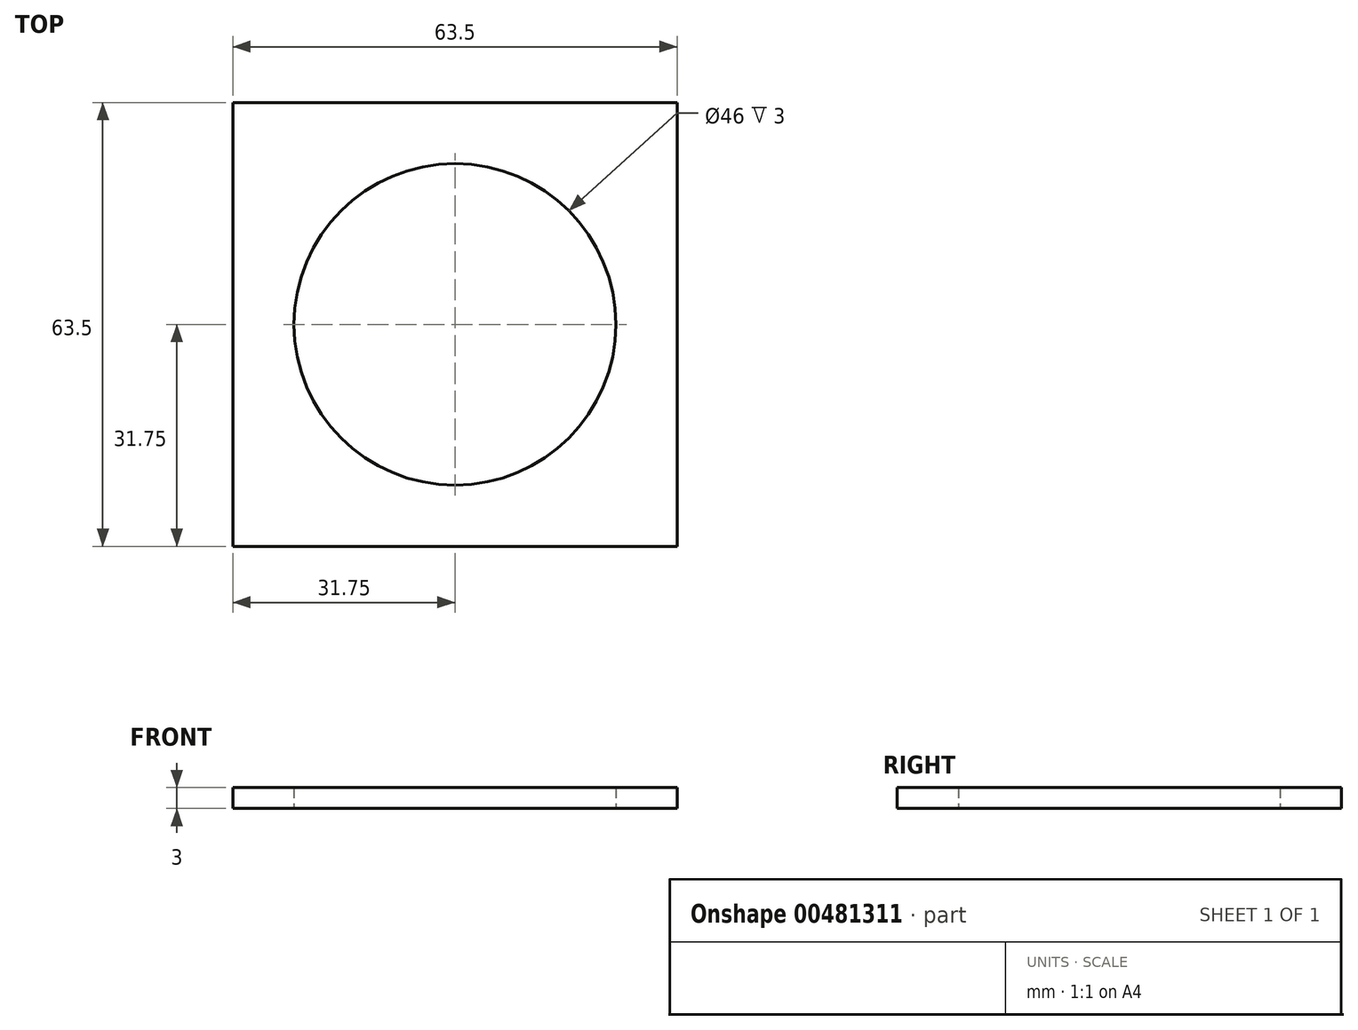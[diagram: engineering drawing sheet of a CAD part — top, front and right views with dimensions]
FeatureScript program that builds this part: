
annotation { "Feature Type Name" : "Feature", "Feature Type Description" : "" }
export const myFeature = defineFeature(function(context is Context, id is Id, definition is map)
    precondition{}
    {
        {
            var Q0;
            Q0=qCreatedBy(makeId("Top.planeOp"),FACE);
            var sketch = newSketch(context, id + "F0", { "sketchPlane" : qUnion([Q0])});
            skCircle(sketch, "E0", {"center": v(0, 0) * mm, "radius": 23 * mm});
            skLineSegment(sketch, "E1.bottom", {"start": v(31.75, 31.75) * mm, "end": v(-31.75, 31.75) * mm});
            skLineSegment(sketch, "E1.top", {"start": v(31.75, -31.75) * mm, "end": v(-31.75, -31.75) * mm});
            skLineSegment(sketch, "E1.left", {"start": v(31.75, 31.75) * mm, "end": v(31.75, -31.75) * mm});
            skLineSegment(sketch, "E1.right", {"start": v(-31.75, 31.75) * mm, "end": v(-31.75, -31.75) * mm});
            skSolve(sketch);
        }
        {
            var Q0;
            Q0=makeQuery(id+"F0.imprint","IMPRINT",FACE,{"disambiguationData":[TD([[makeQuery(id+"F0.imprint","IMPRINT",EDGE,{"derivedFrom":sQuery(id+"F0.wireOp",EDGE,"E0")}),-1.0]])]});
            extrude(context, id + "F1", {"entities" : qUnion([Q0]), "depth" : 3 * mm});
        }
    });
